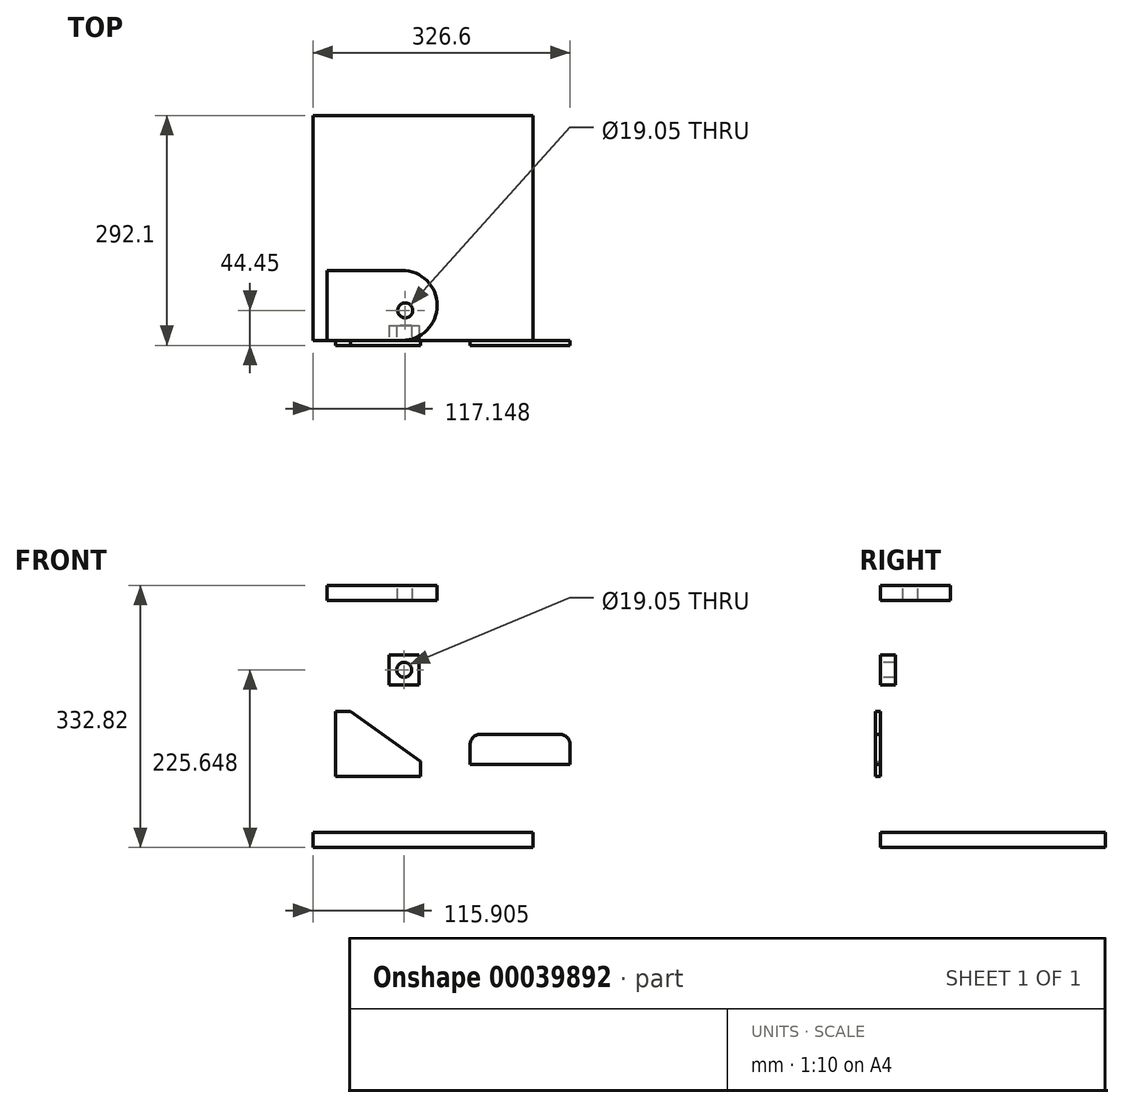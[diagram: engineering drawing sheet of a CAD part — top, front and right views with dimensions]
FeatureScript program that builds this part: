
annotation { "Feature Type Name" : "Feature", "Feature Type Description" : "" }
export const myFeature = defineFeature(function(context is Context, id is Id, definition is map)
    precondition{}
    {
        {
            var Q0;
            Q0=qCreatedBy(makeId("Front.planeOp"),FACE);
            var sketch = newSketch(context, id + "F0", { "sketchPlane" : qUnion([Q0])});
            skLineSegment(sketch, "E0", {"start": v(-50.86, 45.74) * mm, "end": v(-50.86, -36.8) * mm});
            skLineSegment(sketch, "E1", {"start": v(-50.86, -36.8) * mm, "end": v(57.1, -36.8) * mm});
            skLineSegment(sketch, "E2", {"start": v(57.1, -36.8) * mm, "end": v(57.1, -17.76) * mm});
            skLineSegment(sketch, "E3", {"start": v(57.1, -17.76) * mm, "end": v(-31.8, 45.74) * mm});
            skLineSegment(sketch, "E4", {"start": v(-31.8, 45.74) * mm, "end": v(-50.86, 45.74) * mm});
            skLineSegment(sketch, "E5.rect.bottom", {"start": v(73.02, 19.05) * mm, "end": v(200.02, 19.05) * mm});
            skLineSegment(sketch, "E5.rect.top", {"start": v(73.02, -19.05) * mm, "end": v(200.02, -19.05) * mm});
            skLineSegment(sketch, "E5.rect.left", {"start": v(73.02, 19.05) * mm, "end": v(73.02, -19.05) * mm});
            skLineSegment(sketch, "E5.rect.right", {"start": v(200.02, 19.05) * mm, "end": v(200.02, -19.05) * mm});
            skPoint(sketch, "E5.rect.middle", {"position": v(136.52, 0) * mm});
            skSolve(sketch);
        }
        {
            var Q0;
            Q0=makeQuery(id+"F0.imprint","IMPRINT",FACE,{"disambiguationData":[TD([[makeQuery(id+"F0.imprint","IMPRINT",EDGE,{"derivedFrom":sQuery(id+"F0.wireOp",EDGE,"E0")}),1.0]])]});
            extrude(context, id + "F1", {"entities" : qUnion([Q0]), "depth" : 6.35 * mm});
        }
        {
            var Q0;
            Q0=qCreatedBy(makeId("Front.planeOp"),FACE);
            var sketch = newSketch(context, id + "F2", { "sketchPlane" : qUnion([Q0])});
            skLineSegment(sketch, "E6.rect.bottom", {"start": v(120.1, 16.51) * mm, "end": v(247.1, 16.51) * mm});
            skLineSegment(sketch, "E6.rect.top", {"start": v(120.1, -21.59) * mm, "end": v(247.1, -21.59) * mm});
            skLineSegment(sketch, "E6.rect.left", {"start": v(120.1, 16.51) * mm, "end": v(120.1, -21.59) * mm});
            skLineSegment(sketch, "E6.rect.right", {"start": v(247.1, 16.51) * mm, "end": v(247.1, -21.59) * mm});
            skPoint(sketch, "E6.rect.middle", {"position": v(183.6, -2.54) * mm});
            skSolve(sketch);
        }
        {
            var Q0;
            Q0=makeQuery(id+"F2.imprint","IMPRINT",FACE,{"disambiguationData":[TD([[makeQuery(id+"F2.imprint","IMPRINT",EDGE,{"derivedFrom":sQuery(id+"F2.wireOp",EDGE,"E6.rect.bottom")}),-1.0]])]});
            extrude(context, id + "F3", {"entities" : qUnion([Q0]), "depth" : 6.35 * mm});
        }
        {
            var Q0;
            Q0=makeQuery(id+"F3.opExtrude","SWEPT_EDGE",EDGE,{"disambiguationData":[OSD([sQuery(id+"F2.wireOp",EDGE,"E6.rect.bottom"),sQuery(id+"F2.wireOp",EDGE,"E6.rect.left")])]});
            var Q1;
            Q1=makeQuery(id+"F3.opExtrude","SWEPT_EDGE",EDGE,{"disambiguationData":[OSD([sQuery(id+"F2.wireOp",EDGE,"E6.rect.bottom"),sQuery(id+"F2.wireOp",EDGE,"E6.rect.right")])]});
            fillet(context, id + "F4", {"entities" : qUnion([Q0, Q1]), "radius" : 12.7 * mm, "tangentPropagation" : true, "allowEdgeOverflow" : false});
        }
        {
            var Q0;
            Q0=qCreatedBy(makeId("Front.planeOp"),FACE);
            var sketch = newSketch(context, id + "F5", { "sketchPlane" : qUnion([Q0])});
            skLineSegment(sketch, "E7.rect.bottom", {"start": v(-79.5, -107.98) * mm, "end": v(199.9, -107.98) * mm});
            skLineSegment(sketch, "E7.rect.top", {"start": v(-79.5, -127.03) * mm, "end": v(199.9, -127.03) * mm});
            skLineSegment(sketch, "E7.rect.left", {"start": v(-79.5, -107.98) * mm, "end": v(-79.5, -127.03) * mm});
            skLineSegment(sketch, "E7.rect.right", {"start": v(199.9, -107.98) * mm, "end": v(199.9, -127.03) * mm});
            skPoint(sketch, "E7.rect.middle", {"position": v(60.2, -117.5) * mm});
            skSolve(sketch);
        }
        {
            var Q0;
            Q0 = qSketchRegion(id + "F5", true);
            extrude(context, id + "F6", {"entities" : qUnion([Q0]), "oppositeDirection" : true, "depth" : 285.75 * mm});
        }
        {
            var Q0;
            Q0=qCreatedBy(makeId("Front.planeOp"),FACE);
            var sketch = newSketch(context, id + "F7", { "sketchPlane" : qUnion([Q0])});
            skLineSegment(sketch, "E8.rect.bottom", {"start": v(17.35, 117.67) * mm, "end": v(55.45, 117.67) * mm});
            skLineSegment(sketch, "E8.rect.top", {"start": v(17.35, 79.57) * mm, "end": v(55.45, 79.57) * mm});
            skLineSegment(sketch, "E8.rect.left", {"start": v(17.35, 117.67) * mm, "end": v(17.35, 79.57) * mm});
            skLineSegment(sketch, "E8.rect.right", {"start": v(55.45, 117.67) * mm, "end": v(55.45, 79.57) * mm});
            skPoint(sketch, "E8.rect.middle", {"position": v(36.4, 98.62) * mm});
            skCircle(sketch, "E9", {"center": v(36.4, 98.62) * mm, "radius": 9.53 * mm});
            skSolve(sketch);
        }
        {
            var Q0;
            Q0=makeQuery(id+"F7.imprint","IMPRINT",FACE,{"disambiguationData":[TD([[makeQuery(id+"F7.imprint","IMPRINT",EDGE,{"derivedFrom":sQuery(id+"F7.wireOp",EDGE,"E8.rect.bottom")}),-1.0]])]});
            extrude(context, id + "F8", {"entities" : qUnion([Q0]), "oppositeDirection" : true, "depth" : 19.05 * mm});
        }
        {
            var Q0;
            Q0=qCreatedBy(makeId("Front.planeOp"),FACE);
            var sketch = newSketch(context, id + "F9", { "sketchPlane" : qUnion([Q0])});
            skLineSegment(sketch, "E10.rect.bottom", {"start": v(-61.41, 205.8) * mm, "end": v(78.29, 205.8) * mm});
            skLineSegment(sketch, "E10.rect.top", {"start": v(-61.41, 186.74) * mm, "end": v(78.29, 186.74) * mm});
            skLineSegment(sketch, "E10.rect.left", {"start": v(-61.41, 205.8) * mm, "end": v(-61.41, 186.74) * mm});
            skLineSegment(sketch, "E10.rect.right", {"start": v(78.29, 205.8) * mm, "end": v(78.29, 186.74) * mm});
            skPoint(sketch, "E10.rect.middle", {"position": v(8.44, 196.27) * mm});
            skSolve(sketch);
        }
        {
            var Q0;
            Q0=makeQuery(id+"F9.imprint","IMPRINT",FACE,{"disambiguationData":[TD([[makeQuery(id+"F9.imprint","IMPRINT",EDGE,{"derivedFrom":sQuery(id+"F9.wireOp",EDGE,"E10.rect.bottom")}),-1.0]])]});
            extrude(context, id + "F10", {"entities" : qUnion([Q0]), "oppositeDirection" : true, "depth" : 88.9 * mm});
        }
        {
            var Q0;
            Q0=makeQuery(id+"F10.opExtrude","SWEPT_FACE",FACE,{"disambiguationData":[OSD([sQuery(id+"F9.wireOp",EDGE,"E10.rect.bottom")])]});
            var sketch = newSketch(context, id + "F11", { "sketchPlane" : qUnion([Q0])});
            skCircle(sketch, "E11", {"center": v(37.65, 38.1) * mm, "radius": 9.52 * mm});
            skSolve(sketch);
        }
        {
            var Q0;
            Q0=makeQuery(id+"F11.imprint","IMPRINT",FACE,{"disambiguationData":[TD([[makeQuery(id+"F11.imprint","IMPRINT",EDGE,{"derivedFrom":sQuery(id+"F11.wireOp",EDGE,"E11")}),1.0]])]});
            extrude(context, id + "F12", {"entities" : qUnion([Q0]), "operationType" : NewBodyOperationType.REMOVE, "oppositeDirection" : true, "depth" : 76.2 * mm});
        }
        {
            var Q0;
            Q0=makeQuery(id+"F10.opExtrude","CAP_EDGE",EDGE,{"disambiguationData":[OSD([sQuery(id+"F9.wireOp",EDGE,"E10.rect.right")])],"isStart":true});
            var Q1;
            Q1=makeQuery(id+"F10.opExtrude","CAP_EDGE",EDGE,{"disambiguationData":[OSD([sQuery(id+"F9.wireOp",EDGE,"E10.rect.right")])],"isStart":false});
            fillet(context, id + "F13", {"entities" : qUnion([Q0, Q1]), "radius" : 44.45 * mm, "tangentPropagation" : true, "allowEdgeOverflow" : false});
        }
    });
